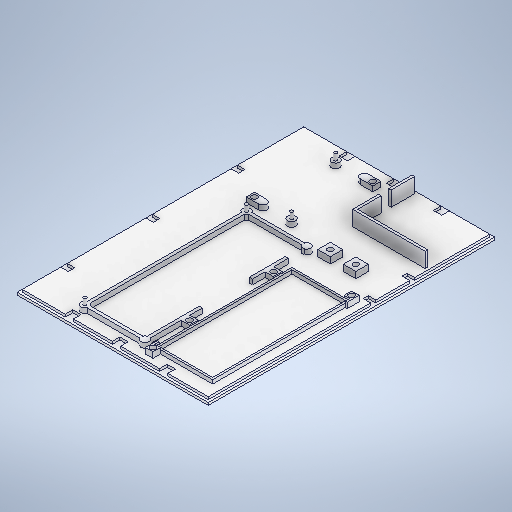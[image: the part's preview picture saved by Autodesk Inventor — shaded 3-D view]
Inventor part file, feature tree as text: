
AUTODESK INVENTOR PART (.ipt)
format: ipt  version: 2025 (Build 290162000, 162)  size: 879,104 bytes
history: native  units: in
note: dims shown in document units (in); Inventor stores cm internally (conversion verified against a paired STEP export)
features: projected_geometry x29, sketch x23, extrude x20, other x2, mirror x1
ambient origin geometry x8: Origin, YZ Plane, XZ Plane, XY Plane, X Axis, Y Axis, Z Axis, Center Point
bodies: Solid1 (feature_tree)
feature tree (75):
  extrude  "BasePlate"  Depth=9.0in
  other  "Template"
  extrude  "SunFounderBase"  Depth=0.2362in
  extrude  "SunfounderStuds"  Depth=0.0984in
  extrude  "RPiBase"  Depth=5.0787in
  extrude  "RPiStuds"  Depth=1.811in
  extrude  "VoltageConverter"  Depth=4.3012in
  extrude  "12VConverter"  Depth=0.0984in
  extrude  "12V2"  Depth=2.2835in
  extrude  "PoEBlock"  Depth=0.0787in
  extrude  "SunfounderSupport"  Depth=0.0787in
  extrude  "Latch12V"  Depth=0.0984in
  extrude  "L12V2"  Depth=0.0984in
  extrude  "LatchRpi"  Depth=0.1969in TaperAngle=0.0deg
  extrude  "LatchSunF"  Depth=0.0787in
  extrude  "LatchSunF2"  Depth=0.0787in
  extrude  "PoERemove"  Depth=0.0984in
  extrude  "EdgeCut"  Depth=0.0984in
  extrude  "LeftCuts"  Depth=0.1969in TaperAngle=0.0deg
  other  "LRMidplane"
  mirror  "RightCuts"
  extrude  "Extrusion24"  Depth=0.3937in
  extrude  "Extrusion25"  Depth=0.8in
  sketch  "Sketch1"  dims[d0=6.0in d1=9.0in]
  projected_geometry  "Projected Loop1"
  sketch  "Sketch3"  dims[d2=0.1575in d3=0.0in d4=0.2362in]
  sketch  "Sketch4"  dims[d6=0.2559in d7=0.0984in]
  projected_geometry  "Projected Loop2"
  projected_geometry  "Projected Loop3"
  projected_geometry  "Projected Loop4"
  projected_geometry  "Projected Loop5"
  sketch  "Sketch5"  dims[d8=1.8898in d9=5.0787in]
  sketch  "Sketch6"  dims[d14=0.1181in d15=1.811in]
  projected_geometry  "Projected Loop6"
  projected_geometry  "Projected Loop7"
  projected_geometry  "Projected Loop8"
  projected_geometry  "Projected Loop9"
  sketch  "Sketch7"  dims[d16=4.3012in d17=1.6325in]
  sketch  "Sketch8"  dims[d29=0.5118in d30=0.0984in]
  projected_geometry  "Projected Loop10"
  projected_geometry  "Projected Loop11"
  sketch  "Sketch9"  dims[d31=0.9055in d32=2.2835in]
  sketch  "Sketch10"  dims[d37=0.0787in d38=0.0787in]
  projected_geometry  "Projected Loop12"
  sketch  "Sketch11"  dims[d39=0.0787in d40=0.0787in]
  sketch  "Sketch14"  dims[d41=0.1575in d42=0.0in d43=0.0984in]
  projected_geometry  "Projected Loop16"
  projected_geometry  "Projected Loop17"
  sketch  "Sketch15"  dims[d44=0.0984in d45=0.0984in]
  projected_geometry  "Projected Loop18"
  sketch  "Sketch16"  dims[d46=0.0984in d47=0.1969in d48=0.0in]
  projected_geometry  "Projected Loop19"
  sketch  "Sketch17"  dims[d49=0.0787in d50=0.0787in]
  projected_geometry  "Projected Loop20"
  projected_geometry  "Projected Loop21"
  sketch  "Sketch18"  dims[d51=0.0787in d52=0.0787in]
  projected_geometry  "Projected Loop22"
  projected_geometry  "Projected Loop23"
  sketch  "Sketch19"  dims[d53=0.1575in d54=0.0in d55=0.0984in]
  projected_geometry  "Projected Loop24"
  projected_geometry  "Projected Loop25"
  sketch  "Sketch20"  dims[d56=0.0984in d57=0.0984in]
  sketch  "Sketch21"  dims[d58=0.0984in d59=0.1969in d60=0.0in]
  projected_geometry  "Projected Loop26"
  projected_geometry  "Projected Loop27"
  sketch  "Sketch22"  dims[d64=0.3937in d65=0.3937in]
  projected_geometry  "Projected Loop28"
  sketch  "Sketch23"  dims[d66=0.1772in d67=0.8in]
  projected_geometry  "Projected Loop29"
  sketch  "Sketch24"  dims[d68=0.3937in]
  projected_geometry  "Projected Loop30"
  sketch  "Sketch25"  dims[d69=0.3937in]
  projected_geometry  "Projected Loop31"
  sketch  "Sketch26"  dims[d70=0.1969in d71=0.0in d72=0.1772in d73=0.1772in d74=0.1969in d75=0.0in d76=0.063in d77=0.063in d78=0.1181in d79=0.0in d80=0.063in d81=0.1969in d82=0.1969in d83=0.1969in d84=0.1969in d85=0.1772in d86=0.0in d87=0.4724in d88=0.0in d96=0.1575in d97=0.0in d98=0.5118in d99=1.5748in d100=0.1969in d101=0.0in d102=0.1732in d103=0.0394in d104=0.2362in d105=0.1732in d106=0.1772in d107=0.0in d108=0.1772in d109=0.1772in d110=0.1969in d111=0.0in d114=2.3591in d115=1.9488in d116=0.0787in d117=0.0787in d118=0.0787in d119=0.3937in d120=0.3937in d121=0.1772in d122=0.1772in d123=0.1575in d124=0.0in d125=0.0394in d126=0.0in d127=1.1811in d128=2.3622in d129=0.2756in d130=0.2756in d131=0.1575in d132=0.0in d133=0.1772in d134=0.1772in d135=0.1969in d136=0.0in d137=0.315in d138=0.1969in d139=0.0in d140=0.0787in d141=0.0787in d142=0.0in d151=0.0787in d152=0.0in d155=1.288in d156=0.2in d157=2.475in d158=0.2in d159=2.475in d160=0.2in d161=0.315in d162=0.315in d163=0.315in d164=0.0787in d165=0.0in d173=0.26in d174=0.6299in d175=0.26in d176=0.6299in d177=0.26in d178=0.6299in d179=0.0787in d180=0.0787in d181=2.5165in d182=0.2362in d183=0.1575in d184=1.063in d185=0.2362in d186=0.1575in d187=0.0787in d188=0.0in]
  projected_geometry  "Projected Loop32"
